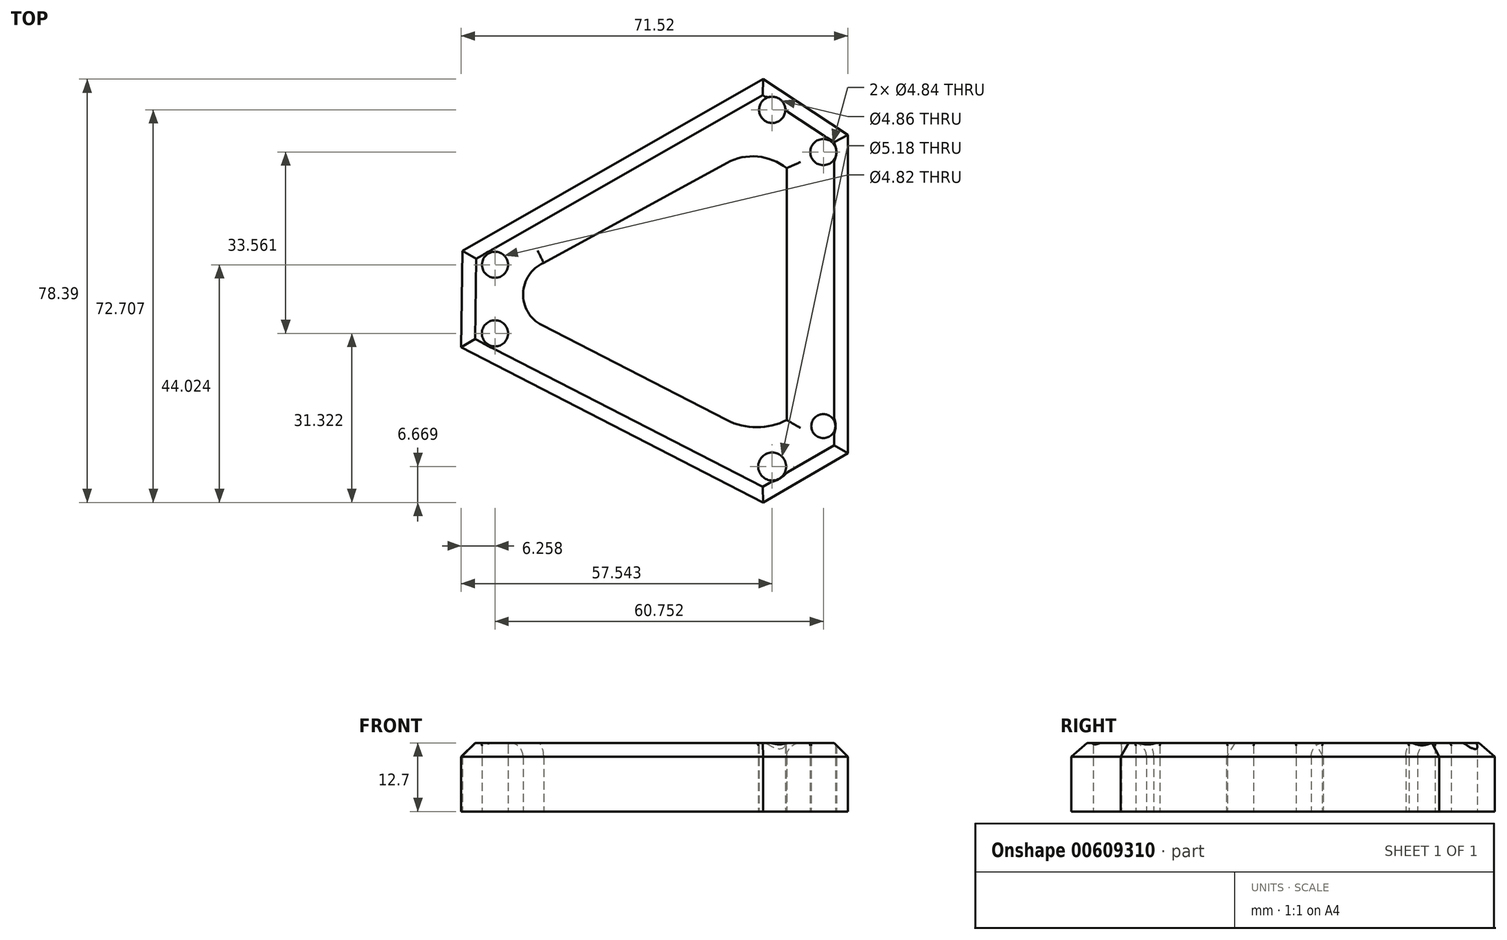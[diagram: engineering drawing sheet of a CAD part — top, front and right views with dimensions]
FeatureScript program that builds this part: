
annotation { "Feature Type Name" : "Feature", "Feature Type Description" : "" }
export const myFeature = defineFeature(function(context is Context, id is Id, definition is map)
    precondition{}
    {
        {
            var Q0;
            Q0=qCreatedBy(makeId("Top.planeOp"),FACE);
            var sketch = newSketch(context, id + "F0", { "sketchPlane" : qUnion([Q0])});
            skLineSegment(sketch, "E0", {"start": v(39.32, 29.9) * mm, "end": v(39.32, -29) * mm});
            skLineSegment(sketch, "E1", {"start": v(39.32, 29.9) * mm, "end": v(23.67, 40.23) * mm});
            skLineSegment(sketch, "E2", {"start": v(39.32, -29) * mm, "end": v(23.67, -38.16) * mm});
            skLineSegment(sketch, "E3", {"start": v(23.67, 40.23) * mm, "end": v(-31.96, 8.45) * mm});
            skLineSegment(sketch, "E4", {"start": v(23.67, -38.16) * mm, "end": v(-32.2, -9.43) * mm});
            skLineSegment(sketch, "E5", {"start": v(-31.96, 8.45) * mm, "end": v(-32.2, -9.43) * mm});
            skLineSegment(sketch, "E6", {"start": v(28.03, 23.73) * mm, "end": v(28.03, -22.89) * mm});
            skLineSegment(sketch, "E7", {"start": v(16.93, 24.72) * mm, "end": v(-16.94, 6.23) * mm});
            skLineSegment(sketch, "E8", {"start": v(16.93, -22.89) * mm, "end": v(-17.28, -5.3) * mm});
            skArc(sketch, "E9", {"start": v(28.03, 23.73) * mm, "mid": v(22.63, 25.9) * mm, "end": v(16.93, 24.72) * mm});
            skArc(sketch, "E10", {"start": v(16.93, -22.89) * mm, "mid": v(22.48, -24.23) * mm, "end": v(28.03, -22.89) * mm});
            skArc(sketch, "E11", {"start": v(-16.94, 6.23) * mm, "mid": v(-20.75, 0.57) * mm, "end": v(-17.28, -5.3) * mm});
            skCircle(sketch, "E12", {"center": v(34.81, -24) * mm, "radius": 2.23 * mm});
            skCircle(sketch, "E13", {"center": v(-25.94, 5.86) * mm, "radius": 2.41 * mm});
            skCircle(sketch, "E14", {"center": v(-25.94, -6.84) * mm, "radius": 2.42 * mm});
            skCircle(sketch, "E15", {"center": v(25.34, -31.5) * mm, "radius": 2.59 * mm});
            skCircle(sketch, "E16", {"center": v(34.81, 26.72) * mm, "radius": 2.42 * mm});
            skCircle(sketch, "E17", {"center": v(25.34, 34.55) * mm, "radius": 2.43 * mm});
            skSolve(sketch);
        }
        {
            var Q0;
            Q0 = qSketchRegion(id + "F0", true);
            extrude(context, id + "F1", {"entities" : qUnion([Q0]), "depth" : 12.7 * mm, "offsetDistance" : 25.4 * mm});
        }
        {
            var Q0;
            Q0=makeQuery(id+"F1.opExtrude","CAP_EDGE",EDGE,{"disambiguationData":[OSD([sQuery(id+"F0.wireOp",EDGE,"E3")])],"isStart":false});
            var Q1;
            Q1=makeQuery(id+"F1.opExtrude","CAP_EDGE",EDGE,{"disambiguationData":[OSD([sQuery(id+"F0.wireOp",EDGE,"E1")])],"isStart":false});
            var Q2;
            Q2=makeQuery(id+"F1.opExtrude","CAP_EDGE",EDGE,{"disambiguationData":[OSD([sQuery(id+"F0.wireOp",EDGE,"E0")])],"isStart":false});
            var Q3;
            Q3=makeQuery(id+"F1.opExtrude","CAP_EDGE",EDGE,{"disambiguationData":[OSD([sQuery(id+"F0.wireOp",EDGE,"E5")])],"isStart":false});
            var Q4;
            Q4=makeQuery(id+"F1.opExtrude","CAP_EDGE",EDGE,{"disambiguationData":[OSD([sQuery(id+"F0.wireOp",EDGE,"E4")])],"isStart":false});
            var Q5;
            Q5=makeQuery(id+"F1.opExtrude","CAP_EDGE",EDGE,{"disambiguationData":[OSD([sQuery(id+"F0.wireOp",EDGE,"E2")])],"isStart":false});
            chamfer(context, id + "F2", {"entities" : qUnion([Q0, Q1, Q2, Q3, Q4, Q5]), "width" : 2.54 * mm, "tangentPropagation" : true});
        }
        {
            var Q0;
            Q0=makeQuery(id+"F1.opExtrude","CAP_EDGE",EDGE,{"disambiguationData":[OSD([sQuery(id+"F0.wireOp",EDGE,"E6")])],"isStart":false});
            var Q1;
            Q1=makeQuery(id+"F1.opExtrude","CAP_EDGE",EDGE,{"disambiguationData":[OSD([sQuery(id+"F0.wireOp",EDGE,"E9")])],"isStart":false});
            var Q2;
            Q2=makeQuery(id+"F1.opExtrude","CAP_EDGE",EDGE,{"disambiguationData":[OSD([sQuery(id+"F0.wireOp",EDGE,"E7")])],"isStart":false});
            var Q3;
            Q3=makeQuery(id+"F1.opExtrude","CAP_EDGE",EDGE,{"disambiguationData":[OSD([sQuery(id+"F0.wireOp",EDGE,"E8")])],"isStart":false});
            fillet(context, id + "F3", {"entities" : qUnion([Q0, Q1, Q2, Q3]), "radius" : 2.54 * mm, "tangentPropagation" : true, "allowEdgeOverflow" : false});
        }
        {
            var Q0;
            Q0=makeQuery(id+"F1.opExtrude","CAP_EDGE",EDGE,{"disambiguationData":[OSD([sQuery(id+"F0.wireOp",EDGE,"E16")])],"isStart":false});
            var Q1;
            Q1=makeQuery(id+"F1.opExtrude","CAP_EDGE",EDGE,{"disambiguationData":[OSD([sQuery(id+"F0.wireOp",EDGE,"E17")])],"isStart":false});
            var Q2;
            Q2=makeQuery(id+"F1.opExtrude","CAP_EDGE",EDGE,{"disambiguationData":[OSD([sQuery(id+"F0.wireOp",EDGE,"E13")])],"isStart":false});
            var Q3;
            Q3=makeQuery(id+"F1.opExtrude","CAP_EDGE",EDGE,{"disambiguationData":[OSD([sQuery(id+"F0.wireOp",EDGE,"E14")])],"isStart":false});
            var Q4;
            Q4=makeQuery(id+"F1.opExtrude","CAP_EDGE",EDGE,{"disambiguationData":[OSD([sQuery(id+"F0.wireOp",EDGE,"E12")])],"isStart":false});
            var Q5;
            Q5=makeQuery(id+"F1.opExtrude","CAP_EDGE",EDGE,{"disambiguationData":[OSD([sQuery(id+"F0.wireOp",EDGE,"E15")])],"isStart":false});
            fillet(context, id + "F4", {"entities" : qUnion([Q0, Q1, Q2, Q3, Q4, Q5]), "radius" : 0.5 * mm, "tangentPropagation" : true, "allowEdgeOverflow" : false});
        }
    });
